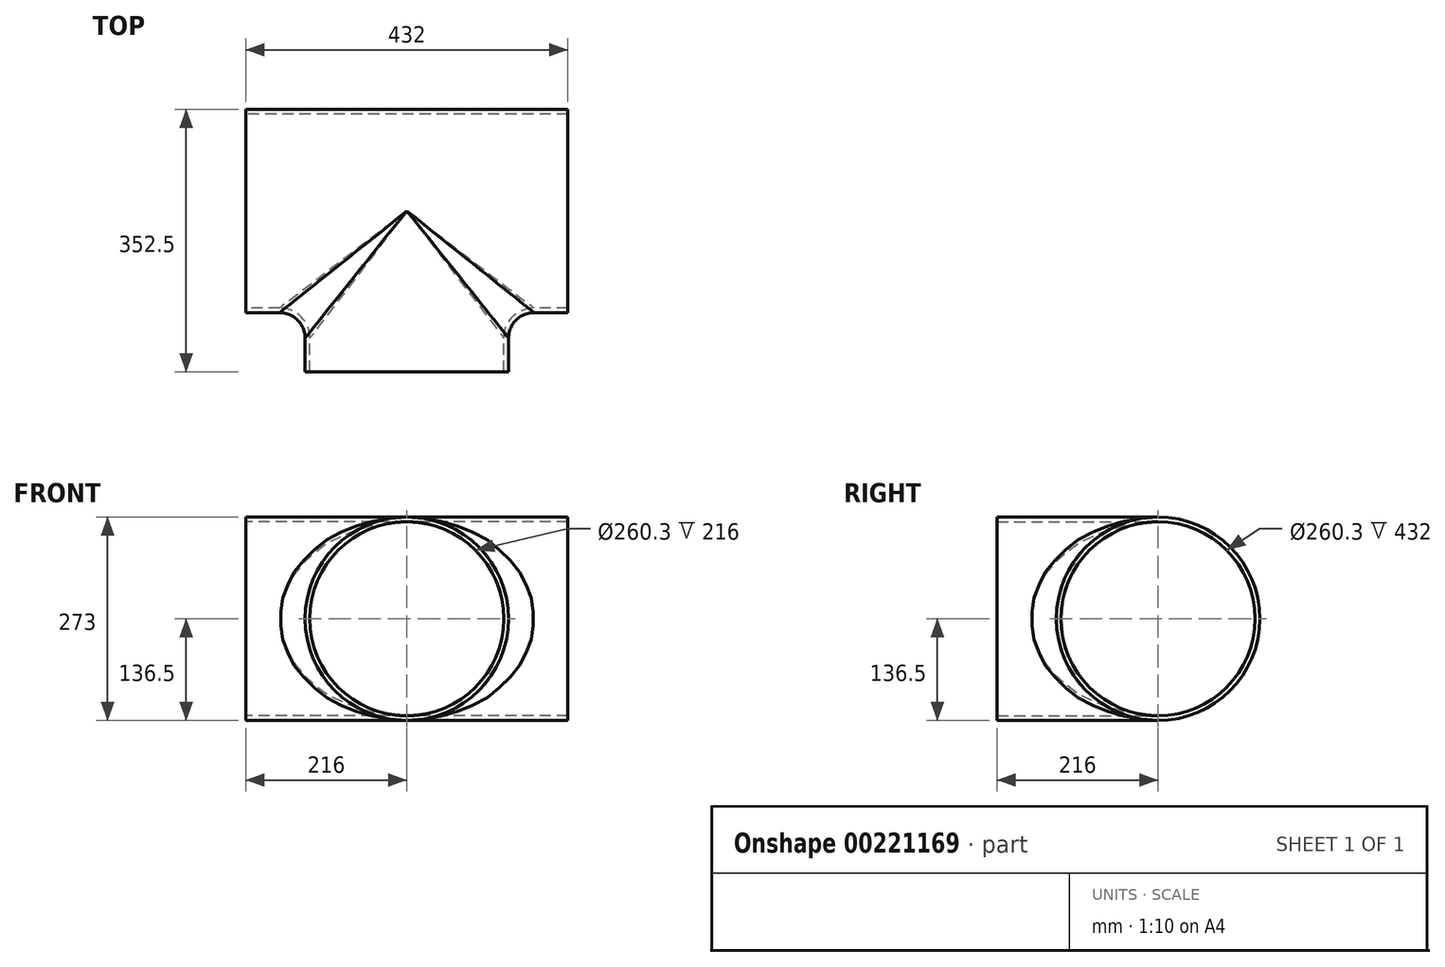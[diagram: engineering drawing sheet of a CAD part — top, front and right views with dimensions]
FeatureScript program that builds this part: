
annotation { "Feature Type Name" : "Feature", "Feature Type Description" : "" }
export const myFeature = defineFeature(function(context is Context, id is Id, definition is map)
    precondition{}
    {
        {
            assignVariable(context, id + "F0", {"name" : "D", "anyValue" : 273});
        }
        {
            assignVariable(context, id + "F1", {"name" : "T", "anyValue" : 6.35});
        }
        {
            assignVariable(context, id + "F2", {"name" : "d", "anyValue" : getVariable(context, 'D')});
        }
        {
            assignVariable(context, id + "F3", {"name" : "A", "anyValue" : 216});
        }
        {
            assignVariable(context, id + "F4", {"name" : "B", "anyValue" : getVariable(context, 'A')});
        }
        {
            var Q0;
            Q0=qCreatedBy(makeId("Right.planeOp"),FACE);
            var sketch = newSketch(context, id + "F5", { "sketchPlane" : qUnion([Q0])});
            skCircle(sketch, "E0", {"center": v(0, 0) * mm, "radius": 136.5 * mm});
            skSolve(sketch);
        }
        {
            var Q0;
            Q0=qCreatedBy(makeId("Front.planeOp"),FACE);
            var sketch = newSketch(context, id + "F6", { "sketchPlane" : qUnion([Q0])});
            skCircle(sketch, "E1", {"center": v(0, 0) * mm, "radius": 136.5 * mm});
            skSolve(sketch);
        }
        {
            var Q0;
            Q0=makeQuery(id+"F5.imprint","IMPRINT",FACE,{"disambiguationData":[TD([[makeQuery(id+"F5.imprint","IMPRINT",EDGE,{"derivedFrom":sQuery(id+"F5.wireOp",EDGE,"E0")}),1.0]])]});
            extrude(context, id + "F7", {"entities" : qUnion([Q0]), "endBound" : BoundingType.SYMMETRIC, "depth" : (2 * getVariable(context, 'A')) * mm});
        }
        {
            var Q0;
            Q0=makeQuery(id+"F6.imprint","IMPRINT",FACE,{"disambiguationData":[TD([[makeQuery(id+"F6.imprint","IMPRINT",EDGE,{"derivedFrom":sQuery(id+"F6.wireOp",EDGE,"E1")}),1.0]])]});
            extrude(context, id + "F8", {"entities" : qUnion([Q0]), "operationType" : NewBodyOperationType.ADD, "depth" : (getVariable(context, 'B')) * mm});
        }
        {
            var Q0;
            Q0=makeQuery(id+"F8.boolean.opBoolean","INTERSECT",EDGE,{"derivedFrom":[makeQuery(id+"F7.opExtrude","SWEPT_FACE",FACE,{"disambiguationData":[OSD([sQuery(id+"F5.wireOp",EDGE,"E0")])]}),makeQuery(id+"F8.opExtrude","SWEPT_FACE",FACE,{"disambiguationData":[OSD([sQuery(id+"F6.wireOp",EDGE,"E1")])]})]});
            fillet(context, id + "F9", {"entities" : qUnion([Q0]), "radius" : (getVariable(context, 'd') / 8) * mm, "tangentPropagation" : true, "allowEdgeOverflow" : false});
        }
        {
            var Q0;
            Q0=makeQuery(id+"F7.opExtrude","CAP_FACE",FACE,{"disambiguationData":[OSD([sQuery(id+"F5.wireOp",EDGE,"E0")])],"isStart":false});
            var Q1;
            Q1=makeQuery(id+"F7.opExtrude","CAP_FACE",FACE,{"disambiguationData":[OSD([sQuery(id+"F5.wireOp",EDGE,"E0")])],"isStart":true});
            var Q2;
            Q2=makeQuery(id+"F8.opExtrude","CAP_FACE",FACE,{"disambiguationData":[OSD([sQuery(id+"F6.wireOp",EDGE,"E1")])],"isStart":false});
            shell(context, id + "F10", {"entities" : qUnion([Q0, Q1, Q2]), "thickness" : (getVariable(context, 'T')) * mm});
        }
        {
            var Q0;
            Q0=qCreatedBy(makeId("Right.planeOp"),FACE);
            var sketch = newSketch(context, id + "F11", { "sketchPlane" : qUnion([Q0])});
            skLineSegment(sketch, "E2", {"start": v(-216, 130.15) * mm, "end": v(-152.4, 123.8) * mm});
            skLineSegment(sketch, "E3", {"start": v(-152.4, 123.8) * mm, "end": v(-216, 123.8) * mm});
            skLineSegment(sketch, "E4", {"start": v(-216, 123.8) * mm, "end": v(-216, 130.15) * mm});
            skLineSegment(sketch, "E5", {"start": v(0, 0) * mm, "end": v(-278.55, 0) * mm, "construction": true});
            skSolve(sketch);
        }
        {
            var Q0;
            Q0=makeQuery(id+"F11.imprint","IMPRINT",FACE,{"disambiguationData":[TD([[makeQuery(id+"F11.imprint","IMPRINT",EDGE,{"derivedFrom":sQuery(id+"F11.wireOp",EDGE,"E2")}),-1.0]])]});
            var Q1;
            Q1=sQuery(id+"F11.wireOp",EDGE,"E5");
            revolve(context, id + "F12", {"operationType" : NewBodyOperationType.REMOVE, "entities" : qUnion([Q0]), "axis" : qUnion([Q1]), "revolveType" : RevolveType.FULL, "oppositeDirection" : true});
        }
    });
